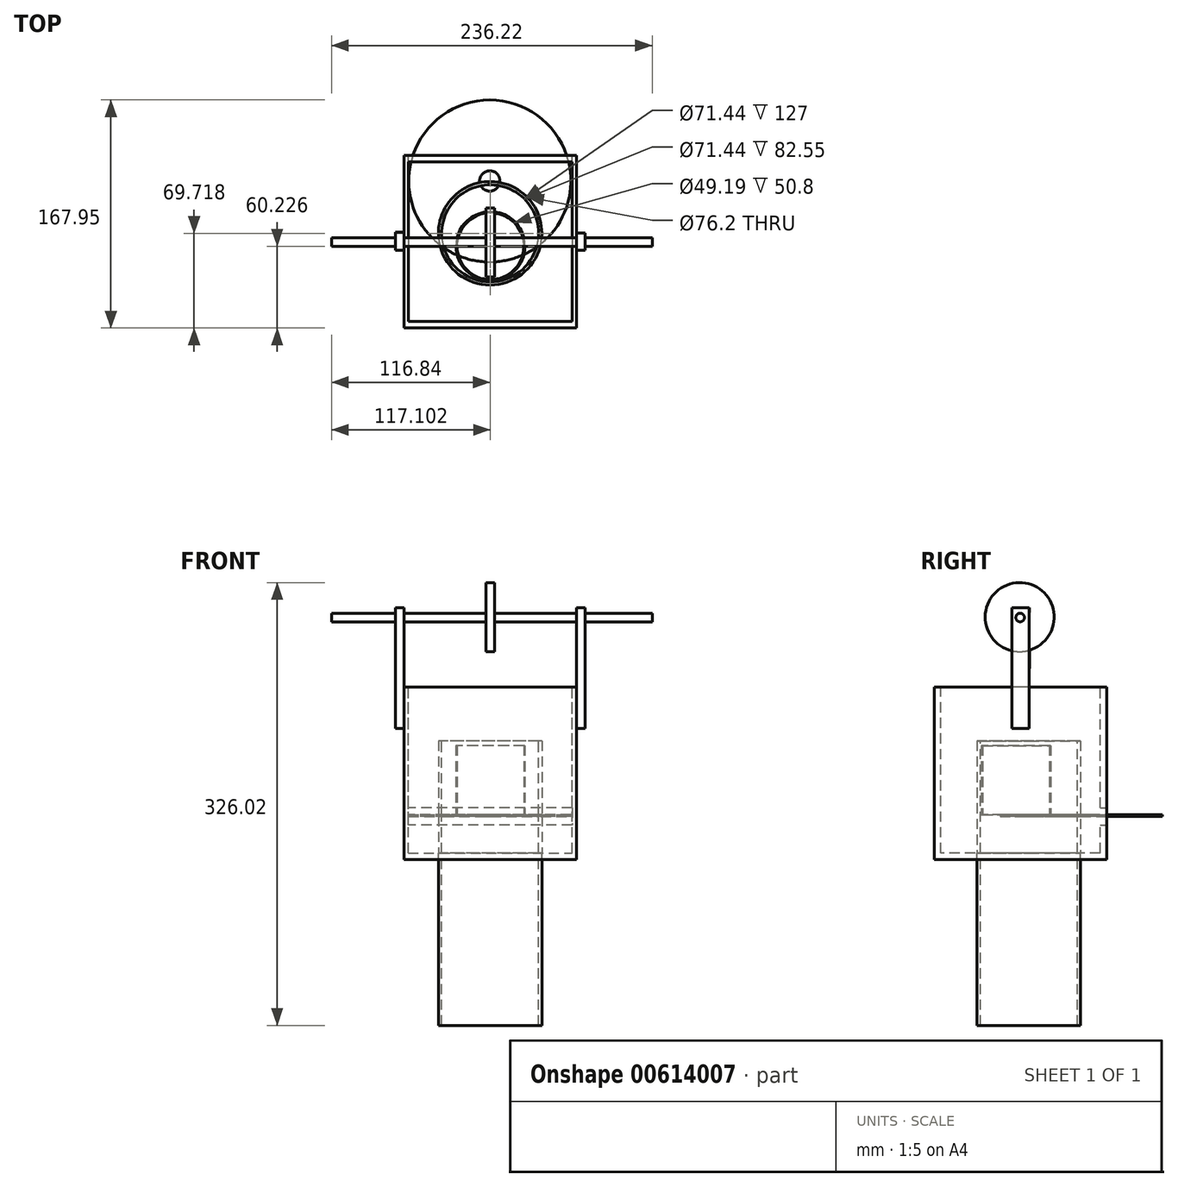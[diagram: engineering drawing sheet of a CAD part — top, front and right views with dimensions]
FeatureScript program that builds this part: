
annotation { "Feature Type Name" : "Feature", "Feature Type Description" : "" }
export const myFeature = defineFeature(function(context is Context, id is Id, definition is map)
    precondition{}
    {
        {
            var Q0;
            Q0=qCreatedBy(makeId("Front.planeOp"),FACE);
            var sketch = newSketch(context, id + "F0", { "sketchPlane" : qUnion([Q0])});
            skLineSegment(sketch, "E0.bottom", {"start": v(0, 0) * mm, "end": v(127, 0) * mm});
            skLineSegment(sketch, "E0.top", {"start": v(0, 127) * mm, "end": v(127, 127) * mm});
            skLineSegment(sketch, "E0.left", {"start": v(0, 0) * mm, "end": v(0, 127) * mm});
            skLineSegment(sketch, "E0.right", {"start": v(127, 0) * mm, "end": v(127, 127) * mm});
            skSolve(sketch);
        }
        {
            var Q0;
            Q0=makeQuery(id+"F0.imprint","IMPRINT",FACE,{"disambiguationData":[TD([[makeQuery(id+"F0.imprint","IMPRINT",EDGE,{"derivedFrom":sQuery(id+"F0.wireOp",EDGE,"E0.bottom")}),1.0]])]});
            extrude(context, id + "F1", {"entities" : qUnion([Q0]), "oppositeDirection" : true, "depth" : 127 * mm, "offsetDistance" : 25.4 * mm});
        }
        {
            var Q0;
            Q0=makeQuery(id+"F1.opExtrude","SWEPT_FACE",FACE,{"disambiguationData":[OSD([sQuery(id+"F0.wireOp",EDGE,"E0.top")])]});
            var sketch = newSketch(context, id + "F2", { "sketchPlane" : qUnion([Q0])});
            skLineSegment(sketch, "E1.bottom", {"start": v(3.17, 122.24) * mm, "end": v(123.83, 122.24) * mm});
            skLineSegment(sketch, "E1.top", {"start": v(3.17, 4.76) * mm, "end": v(123.83, 4.76) * mm});
            skLineSegment(sketch, "E1.left", {"start": v(3.18, 122.24) * mm, "end": v(3.18, 4.76) * mm});
            skLineSegment(sketch, "E1.right", {"start": v(123.83, 122.24) * mm, "end": v(123.83, 4.76) * mm});
            skSolve(sketch);
        }
        {
            var Q0;
            Q0 = qSketchRegion(id + "F2", true);
            extrude(context, id + "F3", {"entities" : qUnion([Q0]), "operationType" : NewBodyOperationType.REMOVE, "oppositeDirection" : true, "depth" : 122.24 * mm, "offsetDistance" : 25.4 * mm});
        }
        {
            var Q0;
            Q0=makeQuery(id+"F1.opExtrude","SWEPT_FACE",FACE,{"disambiguationData":[OSD([sQuery(id+"F0.wireOp",EDGE,"E0.top")])]});
            var sketch = newSketch(context, id + "F4", { "sketchPlane" : qUnion([Q0])});
            skPoint(sketch, "E2.endSnap0", {"position": v(63.5, 4.76) * mm});
            skLineSegment(sketch, "E3", {"start": v(0, 127) * mm, "end": v(0, 88.9) * mm});
            skLineSegment(sketch, "E4", {"start": v(127, 127) * mm, "end": v(127, 78.74) * mm});
            skCircle(sketch, "E5", {"center": v(63.5, 69.72) * mm, "radius": 38.1 * mm});
            skPoint(sketch, "E5.third.point", {"position": v(28.4, 54.9) * mm});
            skSolve(sketch);
        }
        {
            var Q0;
            Q0=makeQuery(id+"F4.imprint","IMPRINT",FACE,{"disambiguationData":[TD([[makeQuery(id+"F4.imprint","IMPRINT",EDGE,{"derivedFrom":sQuery(id+"F4.wireOp",EDGE,"E5")}),1.0]])]});
            extrude(context, id + "F5", {"entities" : qUnion([Q0]), "operationType" : NewBodyOperationType.REMOVE, "oppositeDirection" : true, "depth" : 258.32 * mm, "offsetDistance" : 25.4 * mm});
        }
        {
            var Q0;
            Q0=makeQuery(id+"F3.boolean.opBoolean","COPY",FACE,{"derivedFrom":makeQuery(id+"F3.opExtrude","CAP_FACE",FACE,{"disambiguationData":[OSD([sQuery(id+"F2.wireOp",EDGE,"E1.bottom"),sQuery(id+"F2.wireOp",EDGE,"E1.top"),sQuery(id+"F2.wireOp",EDGE,"E1.left"),sQuery(id+"F2.wireOp",EDGE,"E1.right")])],"isStart":false})});
            var sketch = newSketch(context, id + "F6", { "sketchPlane" : qUnion([Q0])});
            skCircle(sketch, "E6", {"center": v(63.5, 69.72) * mm, "radius": 38.1 * mm});
            skPoint(sketch, "E6.first.point", {"position": v(83.1, 102.39) * mm});
            skPoint(sketch, "E6.second.point", {"position": v(43.85, 37.07) * mm});
            skPoint(sketch, "E6.third.point", {"position": v(87.32, 39.98) * mm});
            skSolve(sketch);
        }
        {
            var Q0;
            Q0 = qSketchRegion(id + "F6", true);
            extrude(context, id + "F7", {"entities" : qUnion([Q0]), "depth" : 82.55 * mm, "offsetDistance" : 25.4 * mm});
        }
        {
            var Q0;
            Q0=makeQuery(id+"F7.opExtrude","CAP_FACE",FACE,{"disambiguationData":[OSD([sQuery(id+"F6.wireOp",EDGE,"E6")])],"isStart":false});
            var sketch = newSketch(context, id + "F8", { "sketchPlane" : qUnion([Q0])});
            skCircle(sketch, "E7", {"center": v(63.5, 69.72) * mm, "radius": 35.72 * mm});
            skSolve(sketch);
        }
        {
            var Q0;
            Q0=makeQuery(id+"F7.opExtrude","CAP_FACE",FACE,{"disambiguationData":[OSD([sQuery(id+"F6.wireOp",EDGE,"E6")])],"isStart":true});
            extrude(context, id + "F9", {"entities" : qUnion([Q0]), "depth" : 127 * mm, "offsetDistance" : 25.4 * mm});
        }
        {
            var Q0;
            Q0=makeQuery(id+"F8.imprint","IMPRINT",FACE,{"disambiguationData":[TD([[makeQuery(id+"F8.imprint","IMPRINT",EDGE,{"derivedFrom":sQuery(id+"F8.wireOp",EDGE,"E7")}),1.0]])]});
            extrude(context, id + "F10", {"entities" : qUnion([Q0]), "operationType" : NewBodyOperationType.REMOVE, "oppositeDirection" : true, "depth" : 222.25 * mm, "offsetDistance" : 25.4 * mm});
        }
        {
            var Q0;
            Q0=makeQuery(id+"F9.opExtrude","CAP_FACE",FACE,{"disambiguationData":[OSD([sQuery(id+"F6.wireOp",EDGE,"E6")])],"isStart":true});
            var sketch = newSketch(context, id + "F11", { "sketchPlane" : qUnion([Q0])});
            skCircle(sketch, "E8", {"center": v(63.5, 69.72) * mm, "radius": 35.72 * mm});
            skSolve(sketch);
        }
        {
            var Q0;
            Q0=makeQuery(id+"F11.imprint","IMPRINT",FACE,{"disambiguationData":[TD([[makeQuery(id+"F11.imprint","IMPRINT",EDGE,{"derivedFrom":sQuery(id+"F11.wireOp",EDGE,"E8")}),1.0]])]});
            extrude(context, id + "F12", {"entities" : qUnion([Q0]), "operationType" : NewBodyOperationType.REMOVE, "oppositeDirection" : true, "depth" : 181.6 * mm, "offsetDistance" : 25.4 * mm});
        }
        {
            var Q0;
            Q0=makeQuery(id+"F1.opExtrude","CAP_FACE",FACE,{"disambiguationData":[OSD([sQuery(id+"F0.wireOp",EDGE,"E0.bottom"),sQuery(id+"F0.wireOp",EDGE,"E0.top"),sQuery(id+"F0.wireOp",EDGE,"E0.left"),sQuery(id+"F0.wireOp",EDGE,"E0.right")])],"isStart":false});
            var sketch = newSketch(context, id + "F13", { "sketchPlane" : qUnion([Q0])});
            skLineSegment(sketch, "E9", {"start": v(-127, 38.1) * mm, "end": v(0, 38.1) * mm});
            skLineSegment(sketch, "E10", {"start": v(-127, 25.4) * mm, "end": v(0, 25.4) * mm});
            skLineSegment(sketch, "E11", {"start": v(0, 25.4) * mm, "end": v(0, 38.1) * mm});
            skLineSegment(sketch, "E12", {"start": v(-127, 38.1) * mm, "end": v(-127, 25.4) * mm});
            skSolve(sketch);
        }
        {
            var Q0;
            Q0 = qSketchRegion(id + "F13", true);
            extrude(context, id + "F14", {"entities" : qUnion([Q0]), "operationType" : NewBodyOperationType.REMOVE, "oppositeDirection" : true, "depth" : 4.76 * mm, "offsetDistance" : 25.4 * mm});
        }
        {
            var Q0;
            Q0=makeQuery(id+"F1.opExtrude","SWEPT_FACE",FACE,{"disambiguationData":[OSD([sQuery(id+"F0.wireOp",EDGE,"E0.right")])]});
            var sketch = newSketch(context, id + "F15", { "sketchPlane" : qUnion([Q0])});
            skLineSegment(sketch, "E13", {"start": v(122.24, 38.1) * mm, "end": v(127, 38.1) * mm});
            skLineSegment(sketch, "E14", {"start": v(127, 38.1) * mm, "end": v(127, 25.4) * mm});
            skLineSegment(sketch, "E15", {"start": v(127, 25.4) * mm, "end": v(122.24, 25.4) * mm});
            skLineSegment(sketch, "E16", {"start": v(122.24, 25.4) * mm, "end": v(122.24, 38.1) * mm});
            skSolve(sketch);
        }
        {
            var Q0;
            Q0 = qSketchRegion(id + "F15", true);
            extrude(context, id + "F16", {"entities" : qUnion([Q0]), "operationType" : NewBodyOperationType.ADD, "oppositeDirection" : true, "depth" : 3.17 * mm, "offsetDistance" : 25.4 * mm});
        }
        {
            var Q0;
            Q0=makeQuery(id+"F1.opExtrude","SWEPT_FACE",FACE,{"disambiguationData":[OSD([sQuery(id+"F0.wireOp",EDGE,"E0.left")])]});
            var sketch = newSketch(context, id + "F17", { "sketchPlane" : qUnion([Q0])});
            skLineSegment(sketch, "E17", {"start": v(-127, 38.1) * mm, "end": v(-122.24, 38.1) * mm});
            skLineSegment(sketch, "E18", {"start": v(-122.24, 38.1) * mm, "end": v(-122.24, 25.4) * mm});
            skLineSegment(sketch, "E19", {"start": v(-122.24, 25.4) * mm, "end": v(-127, 25.4) * mm});
            skLineSegment(sketch, "E20", {"start": v(-127, 25.4) * mm, "end": v(-127, 38.1) * mm});
            skSolve(sketch);
        }
        {
            var Q0;
            Q0=makeQuery(id+"F17.imprint","IMPRINT",FACE,{"disambiguationData":[TD([[makeQuery(id+"F17.imprint","IMPRINT",EDGE,{"derivedFrom":sQuery(id+"F17.wireOp",EDGE,"E17")}),1.0]])]});
            extrude(context, id + "F18", {"entities" : qUnion([Q0]), "operationType" : NewBodyOperationType.ADD, "oppositeDirection" : true, "depth" : 3.17 * mm, "offsetDistance" : 25.4 * mm});
        }
        {
            var Q0;
            Q0=makeQuery(id+"F18.opExtrude","CAP_EDGE",EDGE,{"disambiguationData":[OSD([sQuery(id+"F17.wireOp",EDGE,"E20")])],"isStart":false});
            cPoint(context, id + "F19", {"entities" : qUnion([Q0]), "parameter" : 0.5});
        }
        {
            var Q0;
            Q0=qCreatedBy(makeId("Top.planeOp"),FACE);
            var Q1;
            Q1 = qCreatedBy(id + "F19" ,VERTEX);
            cPlane(context, id + "F20", {"entities" : qUnion([Q0, Q1]), "cplaneType" : CPlaneType.PLANE_POINT, "offset" : 25.4 * mm, "width" : 152.4 * mm, "height" : 152.4 * mm});
        }
        {
            var Q0;
            Q0=qCreatedBy(id+"F20.planeOp",FACE);
            var sketch = newSketch(context, id + "F21", { "sketchPlane" : qUnion([Q0])});
            skCircle(sketch, "E21", {"center": v(63.25, 108.26) * mm, "radius": 59.7 * mm});
            skCircle(sketch, "E22", {"center": v(63.25, 108.26) * mm, "radius": 7.5 * mm});
            skSolve(sketch);
        }
        {
            var Q0;
            Q0=makeQuery(id+"F21.imprint","IMPRINT",FACE,{"disambiguationData":[TD([[makeQuery(id+"F21.imprint","IMPRINT",EDGE,{"derivedFrom":sQuery(id+"F21.wireOp",EDGE,"E21")}),1.0]])]});
            extrude(context, id + "F22", {"entities" : qUnion([Q0]), "operationType" : NewBodyOperationType.ADD, "depth" : 1.2 * mm, "offsetDistance" : 25.4 * mm});
        }
        {
            var Q0;
            {var subQ0=sQuery(id+"F21.wireOp",EDGE,"E21");var subQ1=sQuery(id+"F21.wireOp",EDGE,"E22");Q0=makeQuery(id+"F22.boolean.opBoolean","SPLIT",FACE,{"disambiguationData":[TD([makeQuery(id+"F10.boolean.opBoolean","COPY",FACE,{"derivedFrom":makeQuery(id+"F10.opExtrude","SWEPT_FACE",FACE,{"disambiguationData":[OSD([sQuery(id+"F8.wireOp",EDGE,"E7")])]})})])],"derivedFrom":makeQuery(id+"F22.opExtrude","CAP_FACE",FACE,{"disambiguationData":[OSD([subQ0,subQ1])],"isStart":false})});}
            var sketch = newSketch(context, id + "F23", { "sketchPlane" : qUnion([Q0])});
            skCircle(sketch, "E23", {"center": v(63.76, 60.23) * mm, "radius": 25.4 * mm});
            skCircle(sketch, "E24", {"center": v(63.76, 60.23) * mm, "radius": 24.6 * mm});
            skSolve(sketch);
        }
        {
            var Q0;
            {var subQ0=sQuery(id+"F23.wireOp",EDGE,"E23");var subQ1=sQuery(id+"F21.wireOp",EDGE,"E21");var subQ2=makeQuery(id+"F22.boolean.opBoolean","SPLIT",EDGE,{"disambiguationData":[TD([makeQuery(id+"F10.boolean.opBoolean","COPY",FACE,{"derivedFrom":makeQuery(id+"F10.opExtrude","SWEPT_FACE",FACE,{"disambiguationData":[OSD([sQuery(id+"F8.wireOp",EDGE,"E7")])]})})])],"derivedFrom":makeQuery(id+"F22.opExtrude","CAP_EDGE",EDGE,{"disambiguationData":[OSD([subQ1])],"isStart":false})});var subQ3=makeQuery(id+"F23.imprint","INTERSECT",VERTEX,{"disambiguationData":[OD(0.0)],"derivedFrom":[subQ2,subQ0]});Q0=makeQuery(id+"F23.imprint","IMPRINT",FACE,{"disambiguationData":[TD([[makeQuery(id+"F23.imprint","IMPRINT",EDGE,{"disambiguationData":[TD([[subQ3,1.0]])],"derivedFrom":subQ0}),1.0]])]});}
            var Q1;
            {var subQ0=sQuery(id+"F23.wireOp",EDGE,"E23");var subQ1=sQuery(id+"F21.wireOp",EDGE,"E21");var subQ2=makeQuery(id+"F22.boolean.opBoolean","SPLIT",EDGE,{"disambiguationData":[TD([makeQuery(id+"F10.boolean.opBoolean","COPY",FACE,{"derivedFrom":makeQuery(id+"F10.opExtrude","SWEPT_FACE",FACE,{"disambiguationData":[OSD([sQuery(id+"F8.wireOp",EDGE,"E7")])]})})])],"derivedFrom":makeQuery(id+"F22.opExtrude","CAP_EDGE",EDGE,{"disambiguationData":[OSD([subQ1])],"isStart":false})});var subQ3=makeQuery(id+"F23.imprint","INTERSECT",VERTEX,{"disambiguationData":[OD(0.0)],"derivedFrom":[subQ2,subQ0]});Q1=makeQuery(id+"F23.imprint","IMPRINT",FACE,{"disambiguationData":[TD([[makeQuery(id+"F23.imprint","IMPRINT",EDGE,{"disambiguationData":[TD([[subQ3,-1.0]])],"derivedFrom":subQ0}),1.0]])]});}
            var Q2;
            Q2=sQuery(id+"F23.wireOp",EDGE,"E23");
            extrude(context, id + "F24", {"entities" : qUnion([Q0, Q1]), "surfaceEntities" : qUnion([Q2]), "depth" : 50.8 * mm, "offsetDistance" : 25.4 * mm});
        }
        {
            var Q0;
            Q0=makeQuery(id+"F16.boolean.opBoolean","MERGE",FACE,{"derivedFrom":[makeQuery(id+"F1.opExtrude","SWEPT_FACE",FACE,{"disambiguationData":[OSD([sQuery(id+"F0.wireOp",EDGE,"E0.right")])]}),makeQuery(id+"F16.opExtrude","CAP_FACE",FACE,{"disambiguationData":[OSD([sQuery(id+"F15.wireOp",EDGE,"E13"),sQuery(id+"F15.wireOp",EDGE,"E14"),sQuery(id+"F15.wireOp",EDGE,"E15"),sQuery(id+"F15.wireOp",EDGE,"E16")])],"isStart":true})]});
            var sketch = newSketch(context, id + "F25", { "sketchPlane" : qUnion([Q0])});
            skLineSegment(sketch, "E25", {"start": v(57.15, 127) * mm, "end": v(57.15, 96.52) * mm});
            skLineSegment(sketch, "E26", {"start": v(57.15, 96.52) * mm, "end": v(69.85, 96.52) * mm});
            skLineSegment(sketch, "E27", {"start": v(69.85, 96.52) * mm, "end": v(69.85, 127) * mm});
            skLineSegment(sketch, "E28", {"start": v(69.85, 127) * mm, "end": v(69.85, 185.42) * mm});
            skLineSegment(sketch, "E29", {"start": v(69.85, 185.42) * mm, "end": v(57.15, 185.42) * mm});
            skLineSegment(sketch, "E30", {"start": v(57.15, 185.42) * mm, "end": v(57.15, 127) * mm});
            skSolve(sketch);
        }
        {
            var Q0;
            {var subQ0=sQuery(id+"F25.wireOp",EDGE,"E25");Q0=makeQuery(id+"F25.imprint","IMPRINT",FACE,{"disambiguationData":[TD([[makeQuery(id+"F25.imprint","IMPRINT",EDGE,{"derivedFrom":subQ0}),1.0]])]});}
            var Q1;
            {var subQ0=sQuery(id+"F25.wireOp",EDGE,"E28");Q1=makeQuery(id+"F25.imprint","IMPRINT",FACE,{"disambiguationData":[TD([[makeQuery(id+"F25.imprint","IMPRINT",EDGE,{"derivedFrom":subQ0}),1.0]])]});}
            extrude(context, id + "F26", {"entities" : qUnion([Q0, Q1]), "operationType" : NewBodyOperationType.ADD, "depth" : 6.35 * mm, "offsetDistance" : 25.4 * mm});
        }
        {
            var Q0;
            Q0=makeQuery(id+"F18.boolean.opBoolean","MERGE",FACE,{"derivedFrom":[makeQuery(id+"F1.opExtrude","SWEPT_FACE",FACE,{"disambiguationData":[OSD([sQuery(id+"F0.wireOp",EDGE,"E0.left")])]}),makeQuery(id+"F18.opExtrude","CAP_FACE",FACE,{"disambiguationData":[OSD([sQuery(id+"F17.wireOp",EDGE,"E17"),sQuery(id+"F17.wireOp",EDGE,"E18"),sQuery(id+"F17.wireOp",EDGE,"E19"),sQuery(id+"F17.wireOp",EDGE,"E20")])],"isStart":true})]});
            var sketch = newSketch(context, id + "F27", { "sketchPlane" : qUnion([Q0])});
            skLineSegment(sketch, "E31", {"start": v(-69.85, 127) * mm, "end": v(-69.85, 96.52) * mm});
            skLineSegment(sketch, "E32", {"start": v(-69.85, 96.52) * mm, "end": v(-57.15, 96.52) * mm});
            skLineSegment(sketch, "E33", {"start": v(-57.15, 96.52) * mm, "end": v(-57.15, 127) * mm});
            skLineSegment(sketch, "E34", {"start": v(-57.15, 127) * mm, "end": v(-57.15, 185.42) * mm});
            skLineSegment(sketch, "E35", {"start": v(-57.15, 185.42) * mm, "end": v(-70.42, 185.42) * mm});
            skLineSegment(sketch, "E36", {"start": v(-70.42, 185.42) * mm, "end": v(-69.85, 127) * mm});
            skSolve(sketch);
        }
        {
            var Q0;
            {var subQ0=sQuery(id+"F27.wireOp",EDGE,"E34");Q0=makeQuery(id+"F27.imprint","IMPRINT",FACE,{"disambiguationData":[TD([[makeQuery(id+"F27.imprint","IMPRINT",EDGE,{"derivedFrom":subQ0}),1.0]])]});}
            var Q1;
            {var subQ0=sQuery(id+"F27.wireOp",EDGE,"E31");Q1=makeQuery(id+"F27.imprint","IMPRINT",FACE,{"disambiguationData":[TD([[makeQuery(id+"F27.imprint","IMPRINT",EDGE,{"derivedFrom":subQ0}),1.0]])]});}
            extrude(context, id + "F28", {"entities" : qUnion([Q0, Q1]), "operationType" : NewBodyOperationType.ADD, "depth" : 6.35 * mm, "offsetDistance" : 25.4 * mm});
        }
        {
            var Q0;
            Q0=qCreatedBy(makeId("Right.planeOp"),FACE);
            var sketch = newSketch(context, id + "F29", { "sketchPlane" : qUnion([Q0])});
            skCircle(sketch, "E37", {"center": v(63.25, 178.09) * mm, "radius": 3.18 * mm});
            skSolve(sketch);
        }
        {
            var Q0;
            Q0 = qSketchRegion(id + "F29", true);
            extrude(context, id + "F30", {"entities" : qUnion([Q0]), "operationType" : NewBodyOperationType.ADD, "depth" : 182.88 * mm, "offsetDistance" : 25.4 * mm});
        }
        {
            var Q0;
            Q0 = qSketchRegion(id + "F29", true);
            extrude(context, id + "F31", {"entities" : qUnion([Q0]), "operationType" : NewBodyOperationType.ADD, "oppositeDirection" : true, "depth" : 53.34 * mm, "offsetDistance" : 25.4 * mm});
        }
        {
            var Q0;
            Q0=qCreatedBy(makeId("Right.planeOp"),FACE);
            cPlane(context, id + "F32", {"entities" : qUnion([Q0]), "cplaneType" : CPlaneType.OFFSET, "offset" : 63.5 * mm, "width" : 152.4 * mm, "height" : 152.4 * mm});
        }
        {
            var Q0;
            Q0=qCreatedBy(id+"F32.planeOp",FACE);
            var sketch = newSketch(context, id + "F33", { "sketchPlane" : qUnion([Q0])});
            skCircle(sketch, "E38", {"center": v(62.95, 178.38) * mm, "radius": 25.4 * mm});
            skSolve(sketch);
        }
        {
            var Q0;
            Q0 = qSketchRegion(id + "F33", true);
            extrude(context, id + "F34", {"entities" : qUnion([Q0]), "operationType" : NewBodyOperationType.ADD, "endBound" : BoundingType.SYMMETRIC, "oppositeDirection" : true, "depth" : 6.35 * mm, "offsetDistance" : 25.4 * mm});
        }
    });
